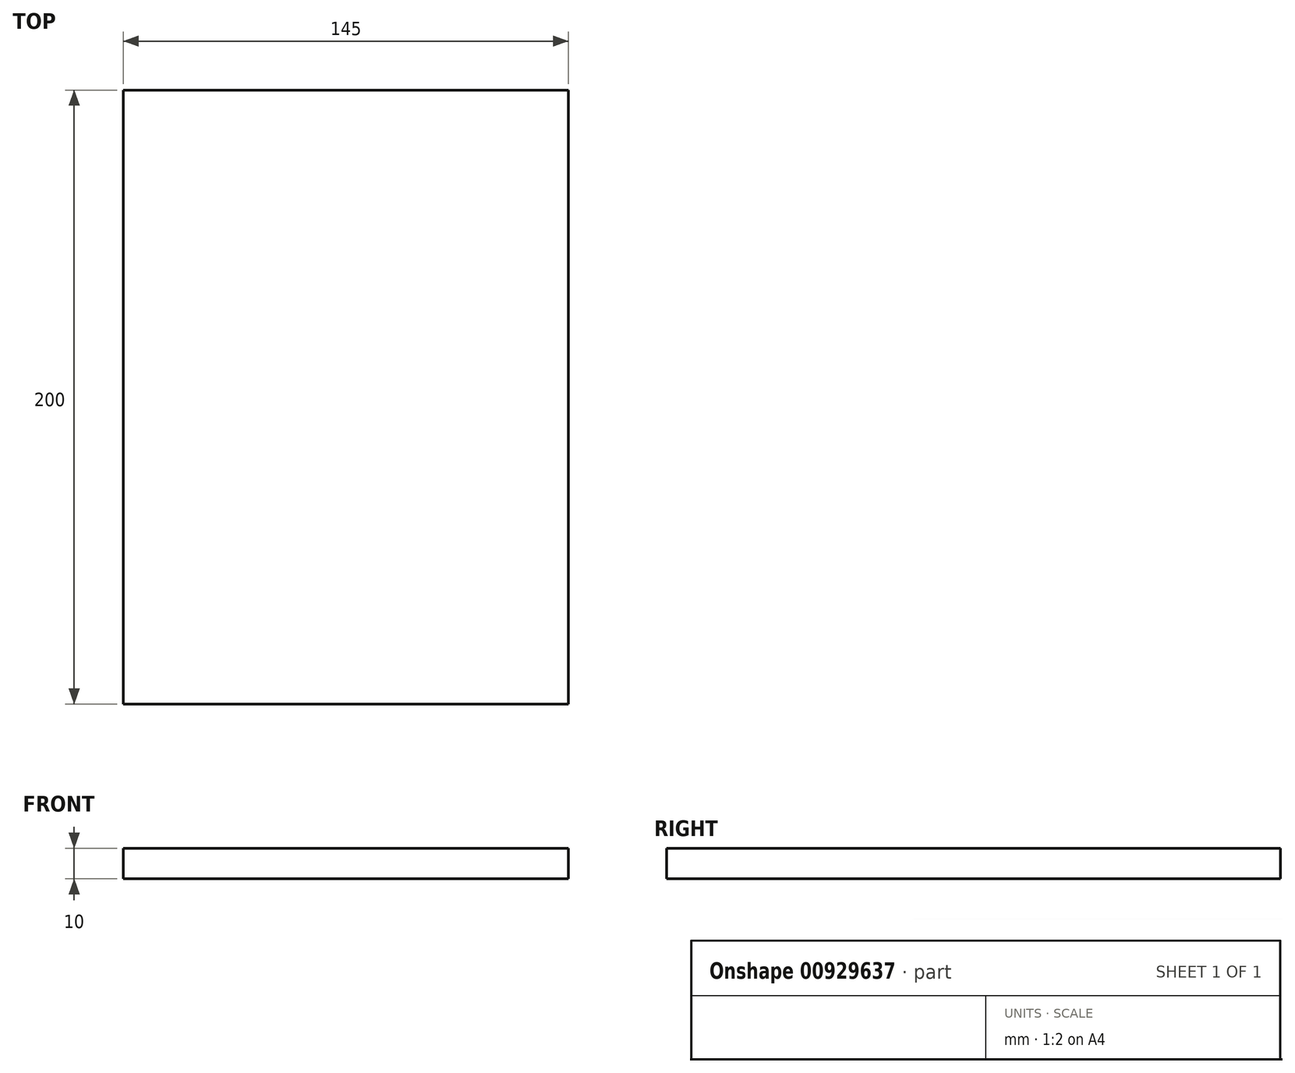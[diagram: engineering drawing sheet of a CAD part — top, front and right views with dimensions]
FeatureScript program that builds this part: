
annotation { "Feature Type Name" : "Feature", "Feature Type Description" : "" }
export const myFeature = defineFeature(function(context is Context, id is Id, definition is map)
    precondition{}
    {
        {
            var Q0;
            Q0=qCreatedBy(makeId("Top.planeOp"),FACE);
            var sketch = newSketch(context, id + "F0", { "sketchPlane" : qUnion([Q0])});
            skLineSegment(sketch, "E0.bottom", {"start": v(0, 0) * mm, "end": v(145, 0) * mm});
            skLineSegment(sketch, "E0.top", {"start": v(0, 200) * mm, "end": v(145, 200) * mm});
            skLineSegment(sketch, "E0.left", {"start": v(0, 0) * mm, "end": v(0, 200) * mm});
            skLineSegment(sketch, "E0.right", {"start": v(145, 0) * mm, "end": v(145, 200) * mm});
            skSolve(sketch);
        }
        {
            var Q0;
            Q0=makeQuery(id+"F0.imprint","IMPRINT",FACE,{"disambiguationData":[TD([[makeQuery(id+"F0.imprint","IMPRINT",EDGE,{"derivedFrom":sQuery(id+"F0.wireOp",EDGE,"E0.bottom")}),1.0]])]});
            extrude(context, id + "F1", {"entities" : qUnion([Q0]), "depth" : 10 * mm, "offsetDistance" : 25 * mm});
        }
    });
